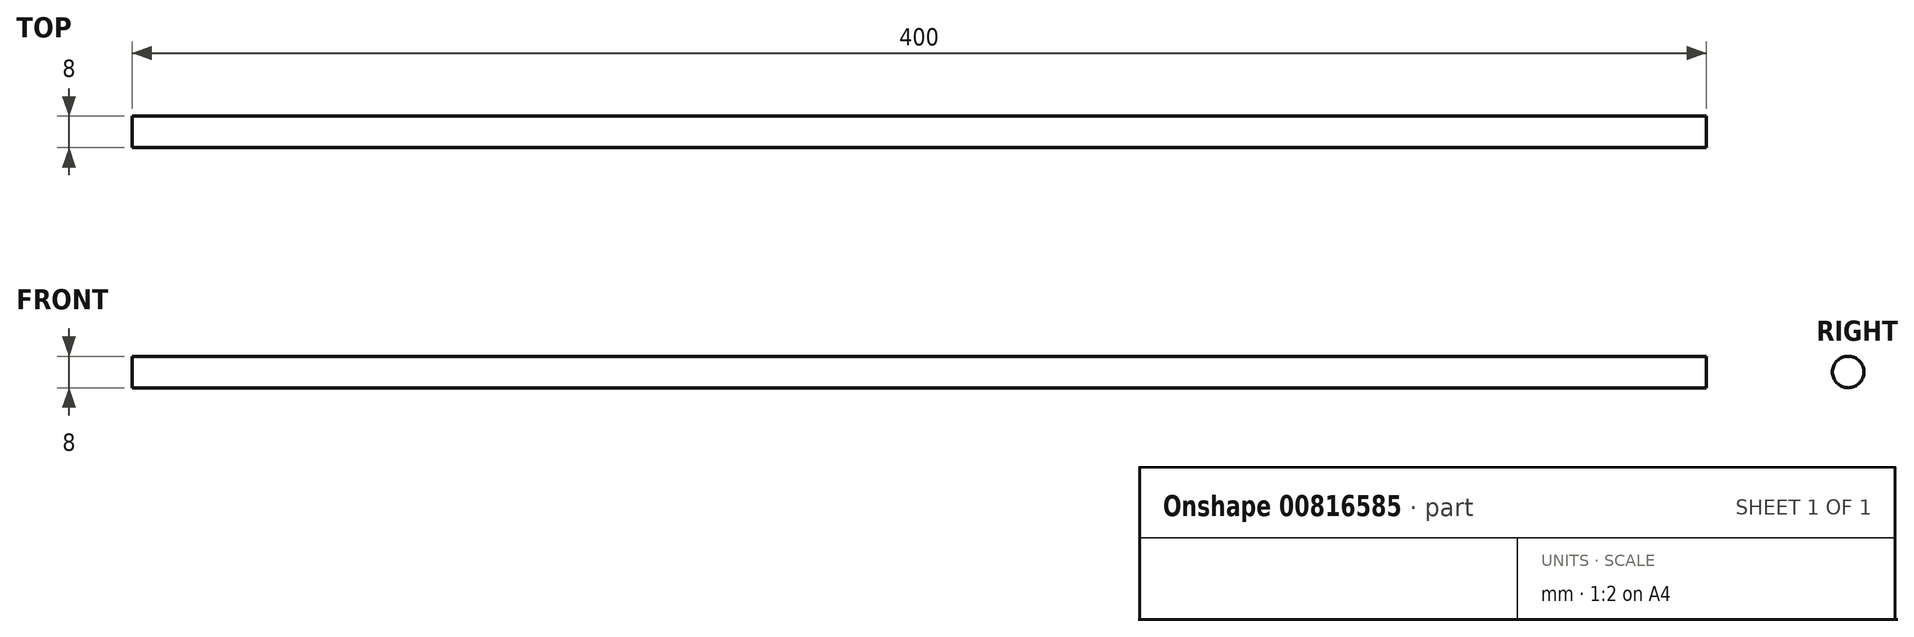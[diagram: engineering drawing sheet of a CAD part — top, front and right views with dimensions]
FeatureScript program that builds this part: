
annotation { "Feature Type Name" : "Feature", "Feature Type Description" : "" }
export const myFeature = defineFeature(function(context is Context, id is Id, definition is map)
    precondition{}
    {
        {
            var Q0;
            Q0=qCreatedBy(makeId("Right.planeOp"),FACE);
            var sketch = newSketch(context, id + "F0", { "sketchPlane" : qUnion([Q0])});
            skCircle(sketch, "E0", {"center": v(0, 0) * mm, "radius": 4 * mm});
            skSolve(sketch);
        }
        {
            var Q0;
            Q0=makeQuery(id+"F0.imprint","IMPRINT",FACE,{"disambiguationData":[TD([[makeQuery(id+"F0.imprint","IMPRINT",EDGE,{"derivedFrom":sQuery(id+"F0.wireOp",EDGE,"E0")}),1.0]])]});
            extrude(context, id + "F1", {"entities" : qUnion([Q0]), "depth" : 400 * mm, "offsetDistance" : 25 * mm});
        }
    });
